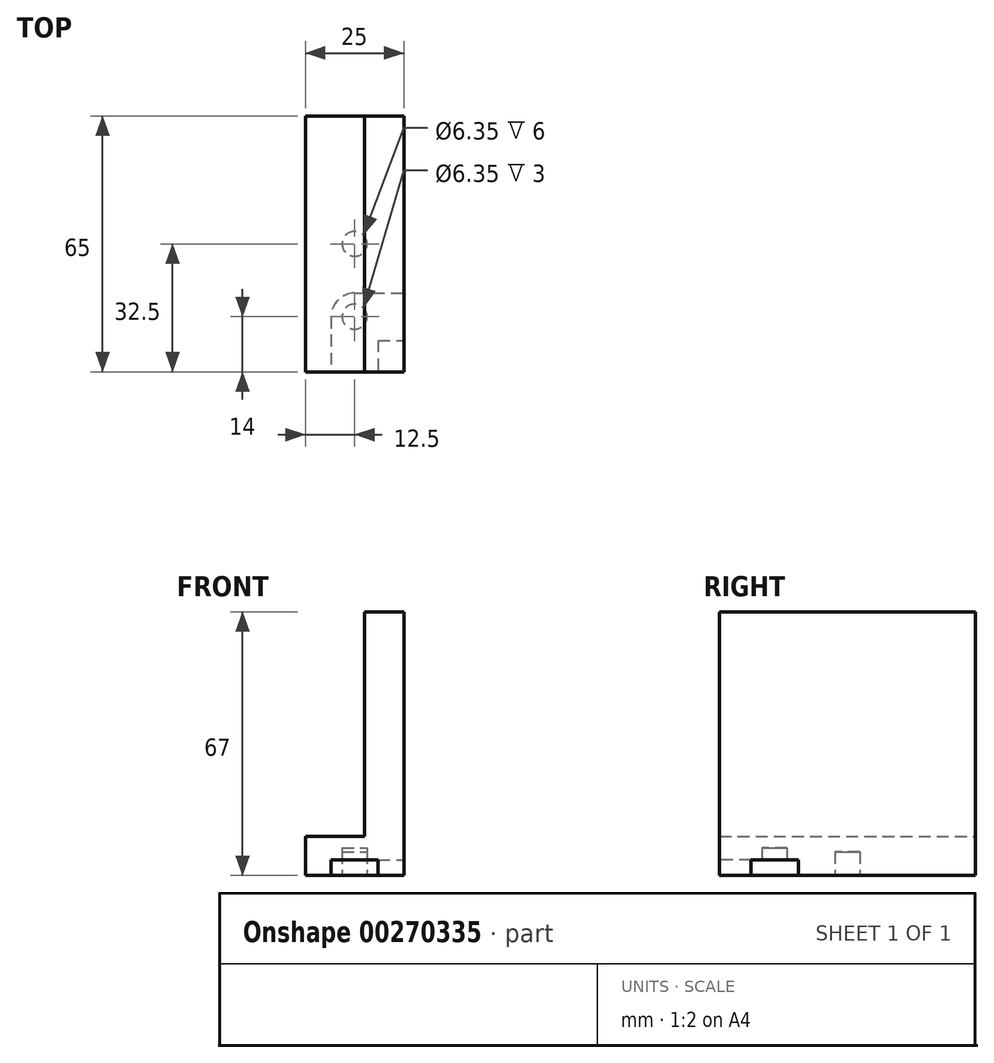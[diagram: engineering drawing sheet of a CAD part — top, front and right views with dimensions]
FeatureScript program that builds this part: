
annotation { "Feature Type Name" : "Feature", "Feature Type Description" : "" }
export const myFeature = defineFeature(function(context is Context, id is Id, definition is map)
    precondition{}
    {
        {
            var Q0;
            Q0=qCreatedBy(makeId("Top.planeOp"),FACE);
            var sketch = newSketch(context, id + "F0", { "sketchPlane" : qUnion([Q0])});
            skLineSegment(sketch, "E0.bottom", {"start": v(12.5, -32.5) * mm, "end": v(-12.5, -32.5) * mm});
            skLineSegment(sketch, "E0.top", {"start": v(12.5, 32.5) * mm, "end": v(-12.5, 32.5) * mm});
            skLineSegment(sketch, "E0.left", {"start": v(12.5, -32.5) * mm, "end": v(12.5, 32.5) * mm});
            skLineSegment(sketch, "E0.right", {"start": v(-12.5, -32.5) * mm, "end": v(-12.5, 32.5) * mm});
            skPoint(sketch, "E0.middle", {"position": v(0, 0) * mm});
            skSolve(sketch);
        }
        {
            var Q0;
            Q0 = qSketchRegion(id + "F0", true);
            extrude(context, id + "F1", {"entities" : qUnion([Q0]), "depth" : 10 * mm});
        }
        {
            var Q0;
            Q0=makeQuery(id+"F1.opExtrude","CAP_FACE",FACE,{"disambiguationData":[OSD([sQuery(id+"F0.wireOp",EDGE,"E0.bottom"),sQuery(id+"F0.wireOp",EDGE,"E0.top"),sQuery(id+"F0.wireOp",EDGE,"E0.left"),sQuery(id+"F0.wireOp",EDGE,"E0.right")])],"isStart":false});
            var sketch = newSketch(context, id + "F2", { "sketchPlane" : qUnion([Q0])});
            skLineSegment(sketch, "E1.bottom", {"start": v(12.5, -32.5) * mm, "end": v(2.5, -32.5) * mm});
            skLineSegment(sketch, "E1.top", {"start": v(12.5, 32.5) * mm, "end": v(2.5, 32.5) * mm});
            skLineSegment(sketch, "E1.left", {"start": v(12.5, -32.5) * mm, "end": v(12.5, 32.5) * mm});
            skLineSegment(sketch, "E1.right", {"start": v(2.5, -32.5) * mm, "end": v(2.5, 32.5) * mm});
            skSolve(sketch);
        }
        {
            var Q0;
            Q0 = qSketchRegion(id + "F2", true);
            extrude(context, id + "F3", {"entities" : qUnion([Q0]), "operationType" : NewBodyOperationType.ADD, "depth" : 57 * mm});
        }
        {
            var Q0;
            Q0=makeQuery(id+"F1.opExtrude","CAP_FACE",FACE,{"disambiguationData":[OSD([sQuery(id+"F0.wireOp",EDGE,"E0.bottom"),sQuery(id+"F0.wireOp",EDGE,"E0.top"),sQuery(id+"F0.wireOp",EDGE,"E0.left"),sQuery(id+"F0.wireOp",EDGE,"E0.right")])],"isStart":true});
            var sketch = newSketch(context, id + "F4", { "sketchPlane" : qUnion([Q0])});
            skCircle(sketch, "E2", {"center": v(0, 0) * mm, "radius": 3.18 * mm});
            skSolve(sketch);
        }
        {
            var Q0;
            Q0 = qSketchRegion(id + "F4", true);
            extrude(context, id + "F5", {"entities" : qUnion([Q0]), "operationType" : NewBodyOperationType.REMOVE, "oppositeDirection" : true, "depth" : 6 * mm});
        }
        {
            var Q0;
            Q0=makeQuery(id+"F1.opExtrude","CAP_FACE",FACE,{"disambiguationData":[OSD([sQuery(id+"F0.wireOp",EDGE,"E0.bottom"),sQuery(id+"F0.wireOp",EDGE,"E0.top"),sQuery(id+"F0.wireOp",EDGE,"E0.left"),sQuery(id+"F0.wireOp",EDGE,"E0.right")])],"isStart":true});
            var sketch = newSketch(context, id + "F6", { "sketchPlane" : qUnion([Q0])});
            skLineSegment(sketch, "E3.bottom", {"start": v(0, 12.5) * mm, "end": v(0, 12.5) * mm});
            skLineSegment(sketch, "E3.top", {"start": v(6, 52.5) * mm, "end": v(-6, 52.5) * mm});
            skLineSegment(sketch, "E3.left", {"start": v(6, 18.5) * mm, "end": v(6, 52.5) * mm});
            skLineSegment(sketch, "E3.right", {"start": v(-6, 18.5) * mm, "end": v(-6, 52.5) * mm});
            skPoint(sketch, "E3.middle", {"position": v(0, 32.5) * mm});
            skPoint(sketch, "E4.visualSharp", {"position": v(-6, 12.5) * mm});
            skArc(sketch, "E4.filletArc", {"start": v(-6, 18.5) * mm, "mid": v(-4.24, 14.26) * mm, "end": v(0, 12.5) * mm});
            skPoint(sketch, "E5.visualSharp", {"position": v(6, 12.5) * mm});
            skArc(sketch, "E5.filletArc", {"start": v(0, 12.5) * mm, "mid": v(4.24, 14.26) * mm, "end": v(6, 18.5) * mm});
            skLineSegment(sketch, "E6", {"start": v(0, 12.5) * mm, "end": v(29.93, 12.5) * mm});
            skLineSegment(sketch, "E7", {"start": v(0, 24.5) * mm, "end": v(29.93, 24.5) * mm});
            skLineSegment(sketch, "E8", {"start": v(29.93, 24.5) * mm, "end": v(29.93, 12.5) * mm});
            skSolve(sketch);
        }
        {
            var Q0;
            Q0 = qSketchRegion(id + "F6", true);
            extrude(context, id + "F7", {"entities" : qUnion([Q0]), "operationType" : NewBodyOperationType.REMOVE, "oppositeDirection" : true, "depth" : 4 * mm});
        }
        {
            var Q0;
            Q0=makeQuery(id+"F7.boolean.opBoolean","COPY",FACE,{"derivedFrom":makeQuery(id+"F7.opExtrude","CAP_FACE",FACE,{"disambiguationData":[OSD([sQuery(id+"F6.wireOp",EDGE,"E3.top"),sQuery(id+"F6.wireOp",EDGE,"E3.left"),sQuery(id+"F6.wireOp",EDGE,"E3.right"),sQuery(id+"F6.wireOp",EDGE,"E4.filletArc"),sQuery(id+"F6.wireOp",EDGE,"E6"),sQuery(id+"F6.wireOp",EDGE,"E7"),sQuery(id+"F6.wireOp",EDGE,"E8")])],"isStart":false})});
            var sketch = newSketch(context, id + "F8", { "sketchPlane" : qUnion([Q0])});
            skCircle(sketch, "E9", {"center": v(0, 18.5) * mm, "radius": 3.17 * mm});
            skSolve(sketch);
        }
        {
            var Q0;
            Q0 = qSketchRegion(id + "F8", true);
            extrude(context, id + "F9", {"entities" : qUnion([Q0]), "operationType" : NewBodyOperationType.REMOVE, "oppositeDirection" : true, "depth" : 3 * mm});
        }
    });
